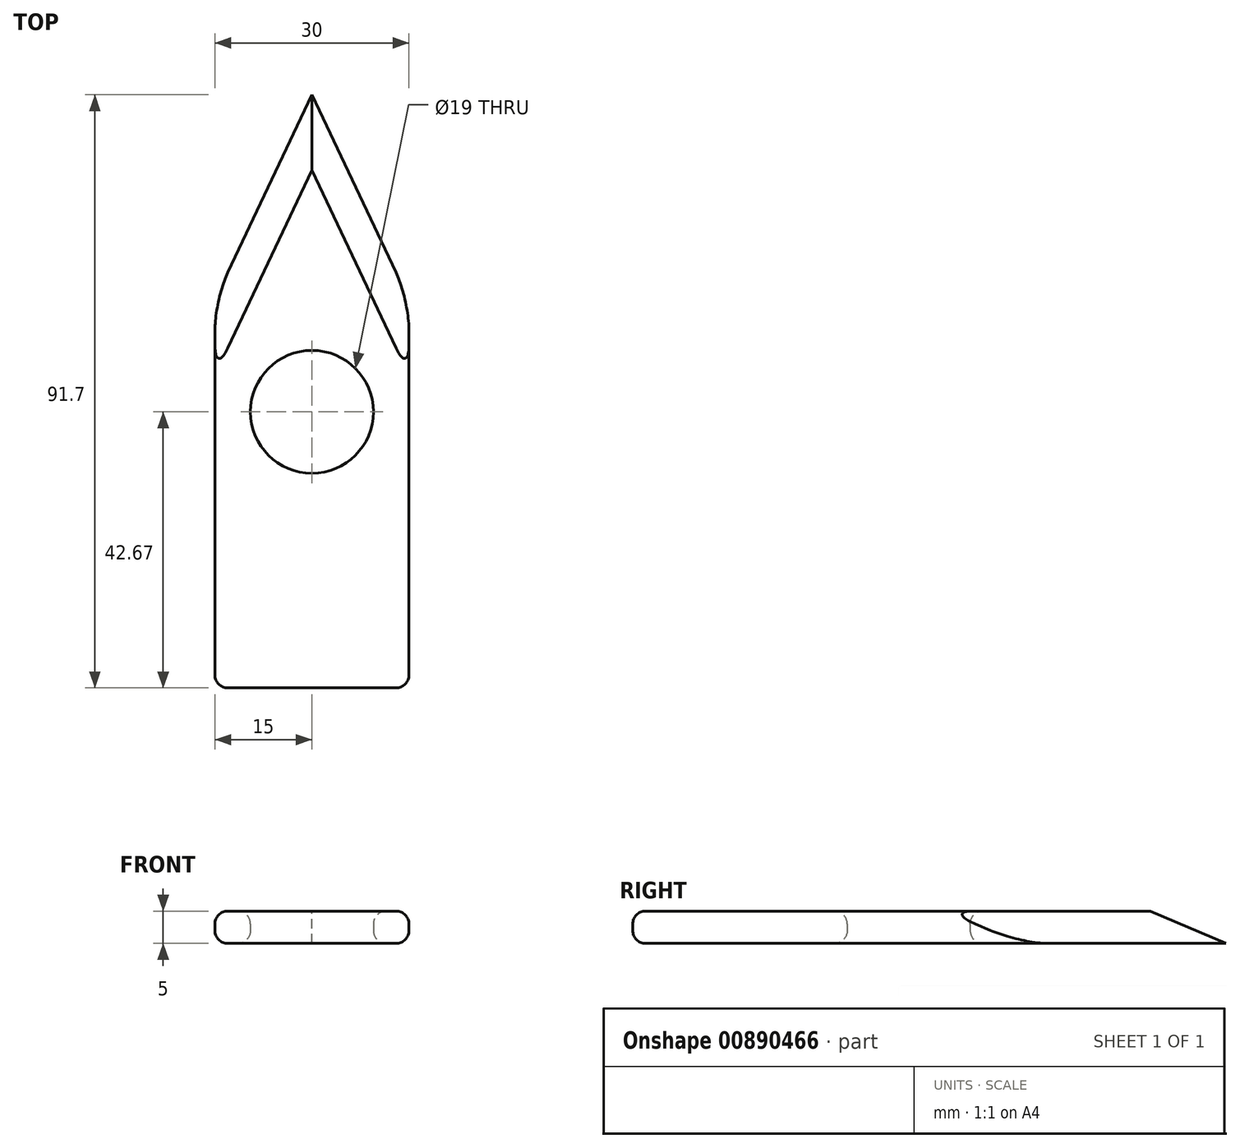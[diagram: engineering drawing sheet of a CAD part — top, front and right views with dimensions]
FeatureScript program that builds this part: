
annotation { "Feature Type Name" : "Feature", "Feature Type Description" : "" }
export const myFeature = defineFeature(function(context is Context, id is Id, definition is map)
    precondition{}
    {
        {
            var Q0;
            Q0=qCreatedBy(makeId("Top.planeOp"),FACE);
            var sketch = newSketch(context, id + "F0", { "sketchPlane" : qUnion([Q0])});
            skCircle(sketch, "E0", {"center": v(0, 0) * mm, "radius": 9.5 * mm});
            skLineSegment(sketch, "E1.bottom", {"start": v(15, 17.33) * mm, "end": v(-15, 17.33) * mm});
            skLineSegment(sketch, "E1.top", {"start": v(15, -42.67) * mm, "end": v(-15, -42.67) * mm});
            skLineSegment(sketch, "E1.left", {"start": v(15, 17.33) * mm, "end": v(15, -42.67) * mm});
            skLineSegment(sketch, "E1.right", {"start": v(-15, 17.33) * mm, "end": v(-15, -42.67) * mm});
            skPoint(sketch, "E1.middle", {"position": v(0, -12.67) * mm});
            skLineSegment(sketch, "E2", {"start": v(-15, 17.33) * mm, "end": v(0, 49.03) * mm});
            skLineSegment(sketch, "E3", {"start": v(0, 49.03) * mm, "end": v(15, 17.33) * mm});
            skSolve(sketch);
        }
        {
            var Q0;
            Q0 = qSketchRegion(id + "F0", true);
            extrude(context, id + "F1", {"entities" : qUnion([Q0]), "depth" : 5 * mm, "offsetDistance" : 25 * mm});
        }
        {
            var Q0;
            Q0=makeQuery(id+"F1.opExtrude","CAP_EDGE",EDGE,{"disambiguationData":[OSD([sQuery(id+"F0.wireOp",EDGE,"E2")])],"isStart":false});
            var Q1;
            Q1=makeQuery(id+"F1.opExtrude","CAP_EDGE",EDGE,{"disambiguationData":[OSD([sQuery(id+"F0.wireOp",EDGE,"E3")])],"isStart":false});
            chamfer(context, id + "F2", {"entities" : qUnion([Q0, Q1]), "width" : 5 * mm, "tangentPropagation" : true});
        }
        {
            var Q0;
            Q0=makeQuery(id+"F1.opExtrude","CAP_EDGE",EDGE,{"disambiguationData":[OSD([sQuery(id+"F0.wireOp",EDGE,"E1.right")])],"isStart":false});
            var Q1;
            Q1=makeQuery(id+"F1.opExtrude","CAP_EDGE",EDGE,{"disambiguationData":[OSD([sQuery(id+"F0.wireOp",EDGE,"E1.left")])],"isStart":false});
            var Q2;
            Q2=makeQuery(id+"F1.opExtrude","CAP_EDGE",EDGE,{"disambiguationData":[OSD([sQuery(id+"F0.wireOp",EDGE,"E1.left")])],"isStart":true});
            var Q3;
            Q3=makeQuery(id+"F1.opExtrude","CAP_EDGE",EDGE,{"disambiguationData":[OSD([sQuery(id+"F0.wireOp",EDGE,"E1.right")])],"isStart":true});
            var Q4;
            Q4=makeQuery(id+"F1.opExtrude","CAP_EDGE",EDGE,{"disambiguationData":[OSD([sQuery(id+"F0.wireOp",EDGE,"E0")])],"isStart":false});
            var Q5;
            Q5=makeQuery(id+"F1.opExtrude","CAP_EDGE",EDGE,{"disambiguationData":[OSD([sQuery(id+"F0.wireOp",EDGE,"E0")])],"isStart":true});
            fillet(context, id + "F3", {"entities" : qUnion([Q0, Q1, Q2, Q3, Q4, Q5]), "radius" : 2 * mm, "tangentPropagation" : true, "allowEdgeOverflow" : false});
        }
        {
            var Q0;
            Q0=makeQuery(id+"F1.opExtrude","CAP_EDGE",EDGE,{"disambiguationData":[OSD([sQuery(id+"F0.wireOp",EDGE,"E1.top")])],"isStart":false});
            fillet(context, id + "F4", {"entities" : qUnion([Q0]), "radius" : 2 * mm, "tangentPropagation" : true, "allowEdgeOverflow" : false});
        }
    });
